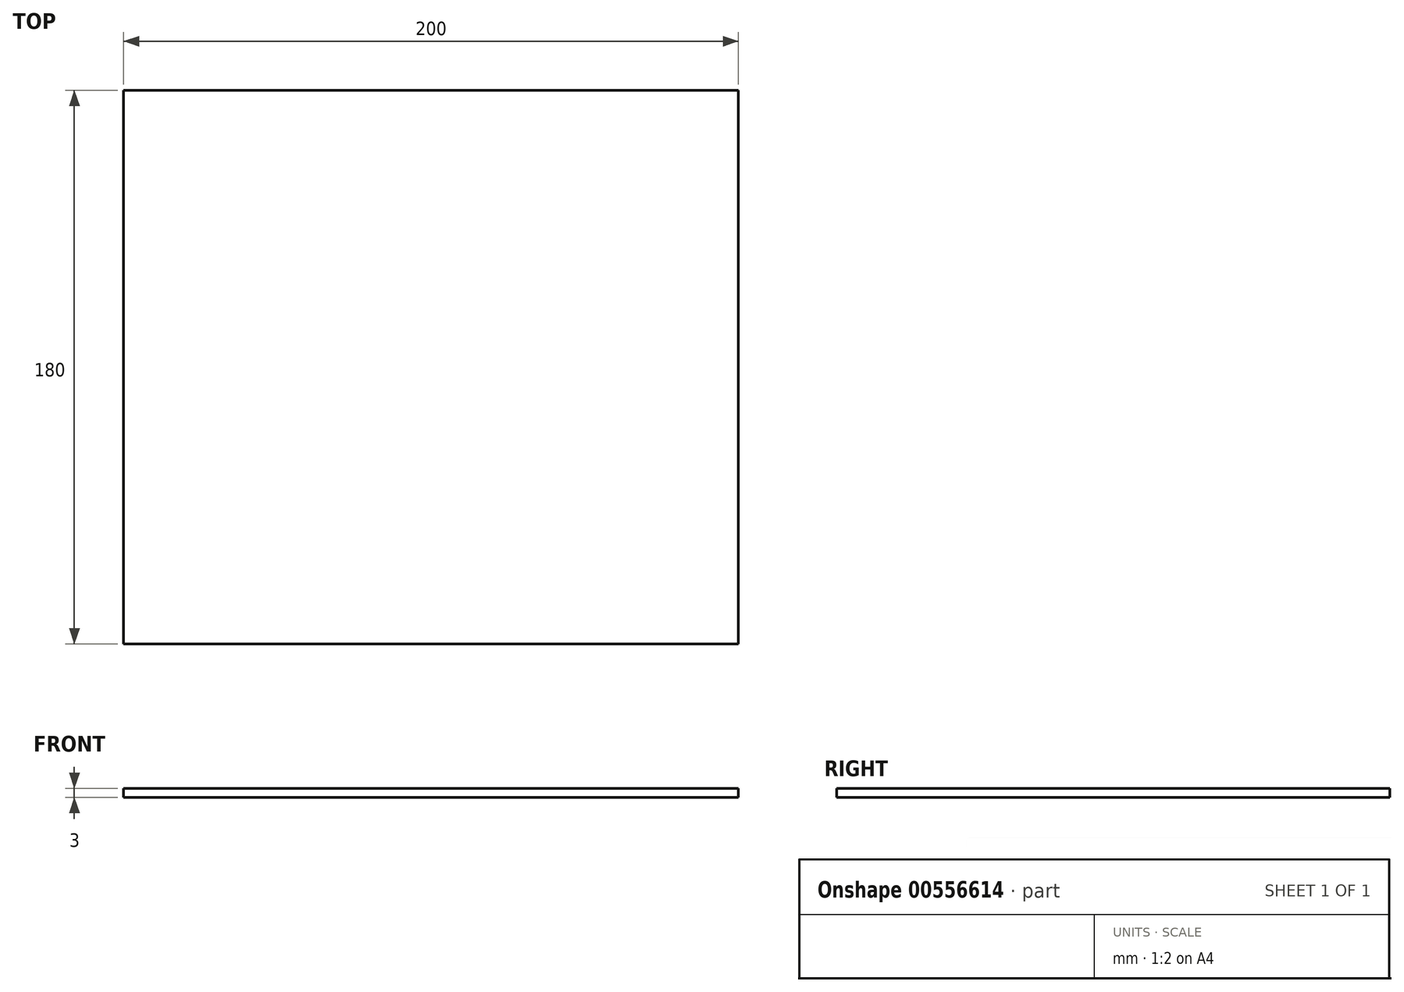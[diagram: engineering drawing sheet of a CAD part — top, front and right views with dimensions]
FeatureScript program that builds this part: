
annotation { "Feature Type Name" : "Feature", "Feature Type Description" : "" }
export const myFeature = defineFeature(function(context is Context, id is Id, definition is map)
    precondition{}
    {
        {
            var Q0;
            Q0=qCreatedBy(makeId("Top.planeOp"),FACE);
            var sketch = newSketch(context, id + "F0", { "sketchPlane" : qUnion([Q0])});
            skLineSegment(sketch, "E0.bottom", {"start": v(-75.35, 105.48) * mm, "end": v(124.65, 105.48) * mm});
            skLineSegment(sketch, "E0.top", {"start": v(-75.35, -74.52) * mm, "end": v(124.65, -74.52) * mm});
            skLineSegment(sketch, "E0.left", {"start": v(-75.35, 105.48) * mm, "end": v(-75.35, -74.52) * mm});
            skLineSegment(sketch, "E0.right", {"start": v(124.65, 105.48) * mm, "end": v(124.65, -74.52) * mm});
            skSolve(sketch);
        }
        {
            var Q0;
            Q0=makeQuery(id+"F0.imprint","IMPRINT",FACE,{"disambiguationData":[TD([[makeQuery(id+"F0.imprint","IMPRINT",EDGE,{"derivedFrom":sQuery(id+"F0.wireOp",EDGE,"E0.bottom")}),-1.0]])]});
            extrude(context, id + "F1", {"entities" : qUnion([Q0]), "depth" : 3 * mm, "offsetDistance" : 25 * mm});
        }
    });
